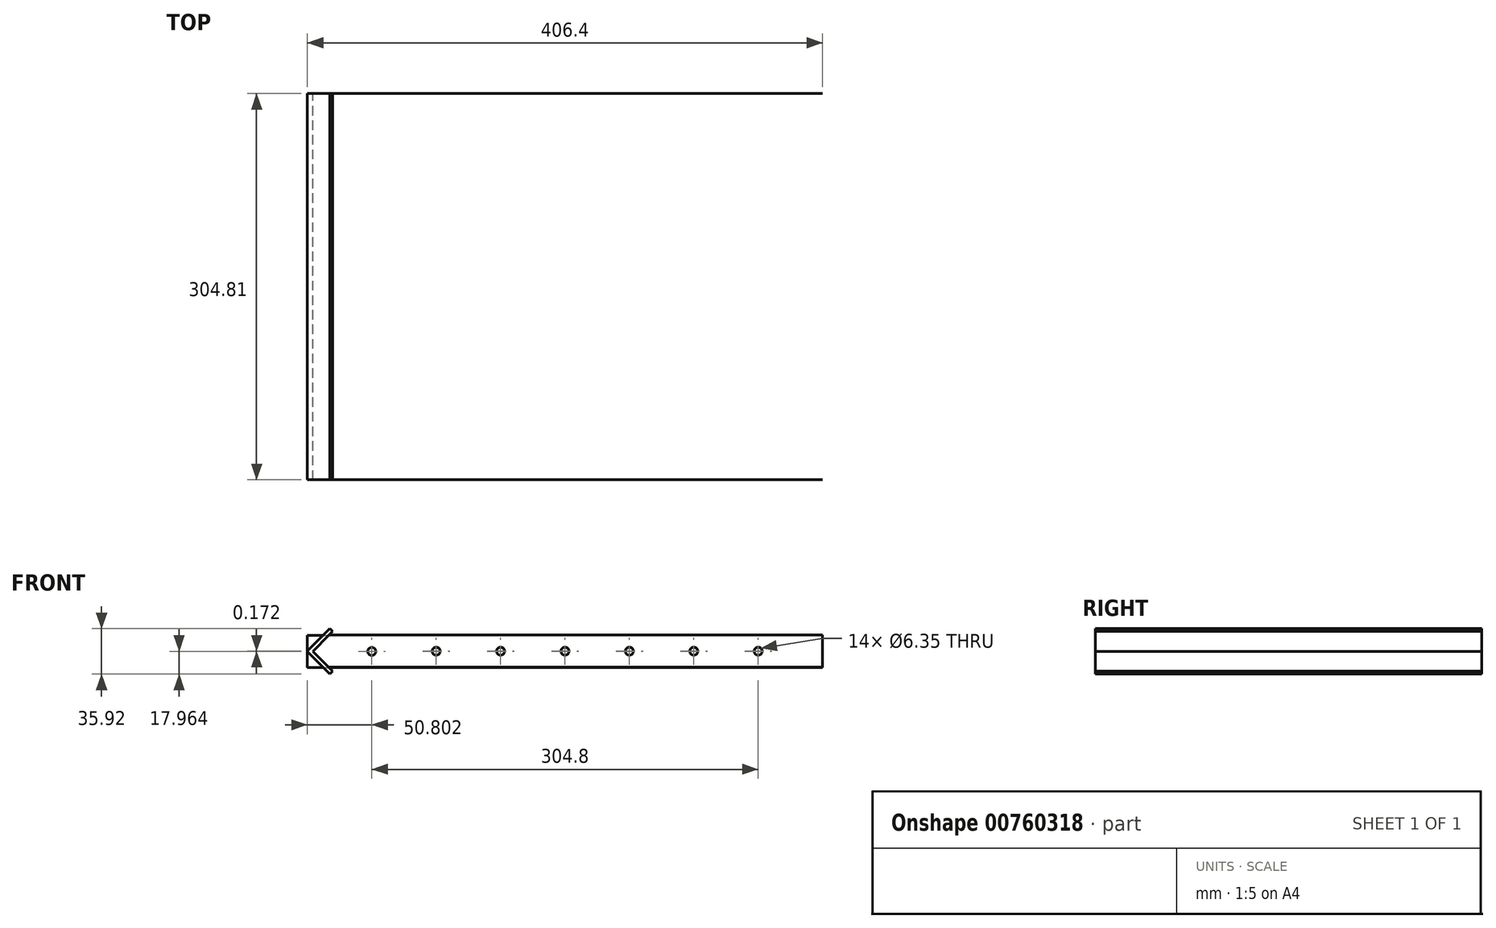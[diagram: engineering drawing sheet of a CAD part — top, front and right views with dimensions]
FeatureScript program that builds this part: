
annotation { "Feature Type Name" : "Feature", "Feature Type Description" : "" }
export const myFeature = defineFeature(function(context is Context, id is Id, definition is map)
    precondition{}
    {
        {
            var Q0;
            Q0=qCreatedBy(makeId("Front.planeOp"),FACE);
            var sketch = newSketch(context, id + "F0", { "sketchPlane" : qUnion([Q0])});
            skLineSegment(sketch, "E0.bottom", {"start": v(-126.28, -15.15) * mm, "end": v(280.12, -15.15) * mm});
            skLineSegment(sketch, "E0.top", {"start": v(-126.28, 10.25) * mm, "end": v(280.12, 10.25) * mm});
            skLineSegment(sketch, "E0.left", {"start": v(-126.28, -15.15) * mm, "end": v(-126.28, 10.25) * mm});
            skLineSegment(sketch, "E0.right", {"start": v(280.12, -15.15) * mm, "end": v(280.12, 10.25) * mm});
            skPoint(sketch, "E1.endSnap0", {"position": v(280.12, -2.45) * mm});
            skCircle(sketch, "E2", {"center": v(76.92, -2.45) * mm, "radius": 3.18 * mm});
            skCircle(sketch, "E3", {"center": v(-24.68, -2.45) * mm, "radius": 3.18 * mm});
            skCircle(sketch, "E4", {"center": v(26.12, -2.45) * mm, "radius": 3.18 * mm});
            skCircle(sketch, "E5", {"center": v(-75.48, -2.45) * mm, "radius": 3.18 * mm});
            skCircle(sketch, "E6", {"center": v(127.72, -2.45) * mm, "radius": 3.18 * mm});
            skCircle(sketch, "E7", {"center": v(178.52, -2.45) * mm, "radius": 3.18 * mm});
            skCircle(sketch, "E8", {"center": v(229.32, -2.45) * mm, "radius": 3.18 * mm});
            skSolve(sketch);
        }
        {
            var Q0;
            Q0=makeQuery(id+"F0.imprint","IMPRINT",FACE,{"disambiguationData":[TD([[makeQuery(id+"F0.imprint","IMPRINT",EDGE,{"derivedFrom":sQuery(id+"F0.wireOp",EDGE,"E0.bottom")}),1.0]])]});
            extrude(context, id + "F1", {"entities" : qUnion([Q0]), "depth" : 1 / 203.2 * mm, "offsetDistance" : 25.4 * mm});
        }
        {
            var Q0;
            Q0=makeQuery(id+"F1.opExtrude","CAP_FACE",FACE,{"disambiguationData":[OSD([sQuery(id+"F0.wireOp",EDGE,"E0.bottom"),sQuery(id+"F0.wireOp",EDGE,"E0.top"),sQuery(id+"F0.wireOp",EDGE,"E0.left"),sQuery(id+"F0.wireOp",EDGE,"E0.right"),sQuery(id+"F0.wireOp",EDGE,"E2"),sQuery(id+"F0.wireOp",EDGE,"E3"),sQuery(id+"F0.wireOp",EDGE,"E4"),sQuery(id+"F0.wireOp",EDGE,"E5"),sQuery(id+"F0.wireOp",EDGE,"E6"),sQuery(id+"F0.wireOp",EDGE,"E7"),sQuery(id+"F0.wireOp",EDGE,"E8")])],"isStart":false});
            var sketch = newSketch(context, id + "F2", { "sketchPlane" : qUnion([Q0])});
            skLineSegment(sketch, "E9", {"start": v(-126.45, -2.45) * mm, "end": v(-108.49, 15.51) * mm});
            skLineSegment(sketch, "E10", {"start": v(-126.45, -2.45) * mm, "end": v(-108.49, -20.4) * mm});
            skLineSegment(sketch, "E11", {"start": v(-108.49, -20.4) * mm, "end": v(-106.24, -18.16) * mm});
            skLineSegment(sketch, "E12", {"start": v(-106.24, -18.16) * mm, "end": v(-121.96, -2.45) * mm});
            skLineSegment(sketch, "E13", {"start": v(-121.96, -2.45) * mm, "end": v(-106.24, 13.27) * mm});
            skLineSegment(sketch, "E14", {"start": v(-106.24, 13.27) * mm, "end": v(-108.49, 15.51) * mm});
            skLineSegment(sketch, "E15", {"start": v(-126.28, 10.25) * mm, "end": v(-126.28, -2.45) * mm});
            skSolve(sketch);
        }
        {
            var Q0;
            {var subQ0=sQuery(id+"F2.wireOp",EDGE,"E14");Q0=makeQuery(id+"F2.imprint","IMPRINT",FACE,{"disambiguationData":[TD([[makeQuery(id+"F2.imprint","IMPRINT",EDGE,{"derivedFrom":subQ0}),1.0]])]});}
            var Q1;
            {var subQ11=sQuery(id+"F2.wireOp",EDGE,"E15");var subQ12=sQuery(id+"F2.wireOp",EDGE,"E9");var subQ13=makeQuery(id+"F2.imprint","INTERSECT",VERTEX,{"derivedFrom":[subQ12,subQ11]});Q1=makeQuery(id+"F2.imprint","IMPRINT",FACE,{"disambiguationData":[TD([[makeQuery(id+"F2.imprint","IMPRINT",EDGE,{"disambiguationData":[TD([[subQ13,-1.0]])],"derivedFrom":subQ12}),-1.0]])]});}
            var Q2;
            {var subQ0=sQuery(id+"F2.wireOp",EDGE,"E11");Q2=makeQuery(id+"F2.imprint","IMPRINT",FACE,{"disambiguationData":[TD([[makeQuery(id+"F2.imprint","IMPRINT",EDGE,{"derivedFrom":subQ0}),1.0]])]});}
            extrude(context, id + "F3", {"entities" : qUnion([Q0, Q1, Q2]), "operationType" : NewBodyOperationType.ADD, "depth" : 304.8 * mm, "offsetDistance" : 25.4 * mm});
        }
        {
            var Q0;
            Q0=makeQuery(id+"F3.opExtrude","CAP_FACE",FACE,{"disambiguationData":[OSD([sQuery(id+"F0.wireOp",EDGE,"E0.left"),sQuery(id+"F2.wireOp",EDGE,"E9"),sQuery(id+"F2.wireOp",EDGE,"E10"),sQuery(id+"F2.wireOp",EDGE,"E11"),sQuery(id+"F2.wireOp",EDGE,"E12"),sQuery(id+"F2.wireOp",EDGE,"E13"),sQuery(id+"F2.wireOp",EDGE,"E14"),sQuery(id+"F2.wireOp",EDGE,"E15")])],"isStart":false});
            var sketch = newSketch(context, id + "F4", { "sketchPlane" : qUnion([Q0])});
            skLineSegment(sketch, "E16", {"start": v(-126.28, -2.27) * mm, "end": v(-126.28, 10.43) * mm});
            skLineSegment(sketch, "E17", {"start": v(-126.28, -2.27) * mm, "end": v(-126.28, -14.97) * mm});
            skLineSegment(sketch, "E18", {"start": v(-126.28, 10.43) * mm, "end": v(-126.28, -14.97) * mm});
            skLineSegment(sketch, "E19", {"start": v(-126.28, 10.43) * mm, "end": v(280.12, 10.43) * mm});
            skLineSegment(sketch, "E20", {"start": v(-126.28, -14.97) * mm, "end": v(280.12, -14.97) * mm});
            skLineSegment(sketch, "E21", {"start": v(280.12, -14.97) * mm, "end": v(280.12, 10.43) * mm});
            skCircle(sketch, "E22", {"center": v(76.92, -2.27) * mm, "radius": 3.18 * mm});
            skCircle(sketch, "E23", {"center": v(178.52, -2.27) * mm, "radius": 3.18 * mm});
            skCircle(sketch, "E24", {"center": v(127.72, -2.27) * mm, "radius": 3.18 * mm});
            skCircle(sketch, "E25", {"center": v(229.32, -2.27) * mm, "radius": 3.18 * mm});
            skCircle(sketch, "E26", {"center": v(26.12, -2.27) * mm, "radius": 3.18 * mm});
            skCircle(sketch, "E27", {"center": v(-24.68, -2.27) * mm, "radius": 3.18 * mm});
            skCircle(sketch, "E28", {"center": v(-75.48, -2.45) * mm, "radius": 3.18 * mm});
            skSolve(sketch);
        }
        {
            var Q0;
            {var subQ0=sQuery(id+"F4.wireOp",EDGE,"E21");Q0=makeQuery(id+"F4.imprint","IMPRINT",FACE,{"disambiguationData":[TD([[makeQuery(id+"F4.imprint","IMPRINT",EDGE,{"derivedFrom":subQ0}),1.0]])]});}
            var Q1;
            {var subQ0=sQuery(id+"F4.wireOp",EDGE,"E18");var subQ1=makeQuery(id+"F3.opExtrude","CAP_EDGE",EDGE,{"disambiguationData":[OSD([sQuery(id+"F2.wireOp",EDGE,"E9")])],"isStart":false});var subQ2=makeQuery(id+"F4.imprint","INTERSECT",VERTEX,{"derivedFrom":[subQ1,subQ0]});var subQ3=sQuery(id+"F4.wireOp",EDGE,"E19");var subQ4=makeQuery(id+"F4.imprint","INTERSECT",VERTEX,{"derivedFrom":[subQ0,subQ3]});Q1=makeQuery(id+"F4.imprint","IMPRINT",FACE,{"disambiguationData":[TD([[makeQuery(id+"F4.imprint","IMPRINT",EDGE,{"disambiguationData":[TD([[subQ2,1.0],[subQ4,-1.0]])],"derivedFrom":subQ0}),1.0]])]});}
            var Q2;
            {var subQ0=sQuery(id+"F4.wireOp",EDGE,"E18");var subQ1=makeQuery(id+"F3.opExtrude","CAP_EDGE",EDGE,{"disambiguationData":[OSD([sQuery(id+"F2.wireOp",EDGE,"E10")])],"isStart":false});var subQ2=makeQuery(id+"F4.imprint","INTERSECT",VERTEX,{"derivedFrom":[subQ1,subQ0]});var subQ3=sQuery(id+"F4.wireOp",EDGE,"E20");var subQ4=makeQuery(id+"F4.imprint","INTERSECT",VERTEX,{"derivedFrom":[subQ0,subQ3]});Q2=makeQuery(id+"F4.imprint","IMPRINT",FACE,{"disambiguationData":[TD([[makeQuery(id+"F4.imprint","IMPRINT",EDGE,{"disambiguationData":[TD([[subQ2,-1.0],[subQ4,1.0]])],"derivedFrom":subQ0}),1.0]])]});}
            var Q3;
            {var subQ0=sQuery(id+"F4.wireOp",EDGE,"E18");var subQ1=makeQuery(id+"F3.opExtrude","CAP_EDGE",EDGE,{"disambiguationData":[OSD([sQuery(id+"F2.wireOp",EDGE,"E9")])],"isStart":false});var subQ2=makeQuery(id+"F4.imprint","INTERSECT",VERTEX,{"derivedFrom":[subQ1,subQ0]});var subQ6=makeQuery(id+"F3.opExtrude","CAP_EDGE",EDGE,{"disambiguationData":[OSD([sQuery(id+"F2.wireOp",EDGE,"E10")])],"isStart":false});var subQ13=makeQuery(id+"F4.imprint","INTERSECT",VERTEX,{"derivedFrom":[subQ6,subQ0]});Q3=makeQuery(id+"F4.imprint","IMPRINT",FACE,{"disambiguationData":[TD([[makeQuery(id+"F4.imprint","IMPRINT",EDGE,{"disambiguationData":[TD([[subQ2,1.0],[subQ13,-1.0]])],"derivedFrom":subQ0}),-1.0]])]});}
            extrude(context, id + "F5", {"entities" : qUnion([Q0, Q1, Q2, Q3]), "operationType" : NewBodyOperationType.ADD, "depth" : 1 / 203.2 * mm, "offsetDistance" : 25.4 * mm});
        }
    });
